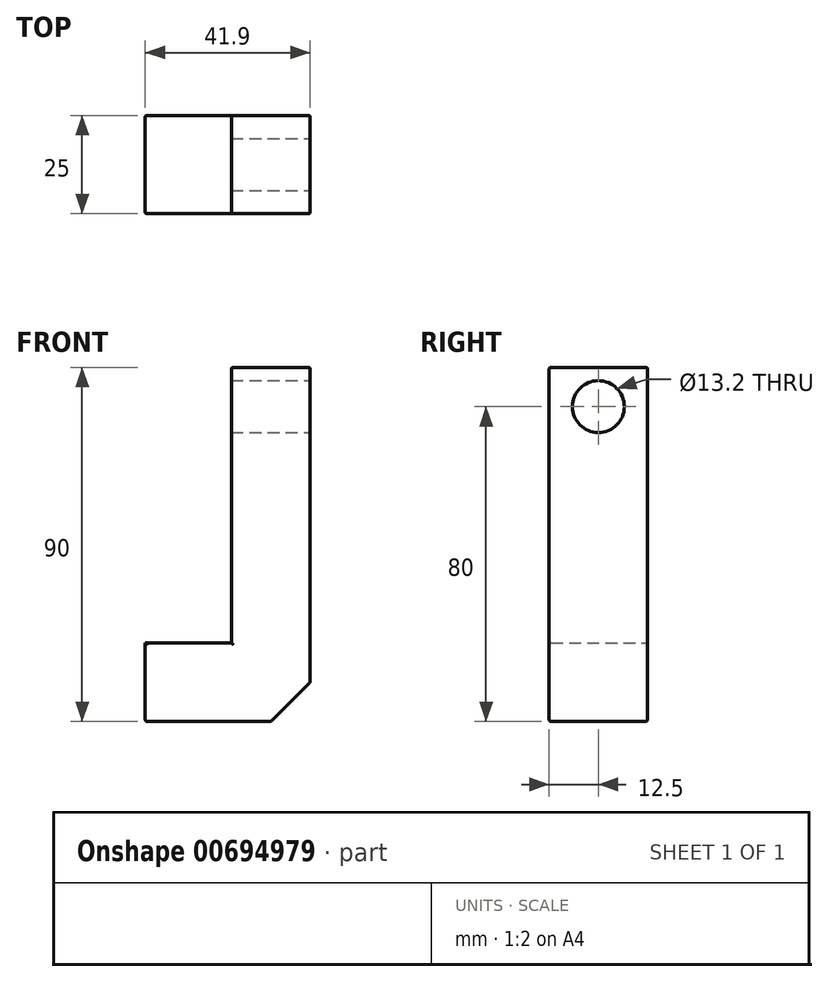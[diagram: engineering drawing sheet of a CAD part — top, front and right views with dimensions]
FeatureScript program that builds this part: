
annotation { "Feature Type Name" : "Feature", "Feature Type Description" : "" }
export const myFeature = defineFeature(function(context is Context, id is Id, definition is map)
    precondition{}
    {
        {
            var Q0;
            Q0=qCreatedBy(makeId("Front.planeOp"),FACE);
            var sketch = newSketch(context, id + "F0", { "sketchPlane" : qUnion([Q0])});
            skLineSegment(sketch, "E0", {"start": v(0, 0) * mm, "end": v(21.9, 0) * mm});
            skLineSegment(sketch, "E1", {"start": v(21.9, 0) * mm, "end": v(21.9, 70) * mm});
            skLineSegment(sketch, "E2", {"start": v(41.9, 70) * mm, "end": v(21.9, 70) * mm});
            skLineSegment(sketch, "E3", {"start": v(41.9, 70) * mm, "end": v(41.9, -20) * mm});
            skLineSegment(sketch, "E4", {"start": v(41.9, -20) * mm, "end": v(0, -20) * mm});
            skLineSegment(sketch, "E5", {"start": v(0, -20) * mm, "end": v(0, 0) * mm});
            skSolve(sketch);
        }
        {
            var Q0;
            Q0=makeQuery(id+"F0.imprint","IMPRINT",FACE,{"disambiguationData":[TD([[makeQuery(id+"F0.imprint","IMPRINT",EDGE,{"derivedFrom":sQuery(id+"F0.wireOp",EDGE,"E0")}),-1.0]])]});
            extrude(context, id + "F1", {"entities" : qUnion([Q0]), "depth" : 25 * mm, "offsetDistance" : 25 * mm});
        }
        {
            var Q0;
            Q0=makeQuery(id+"F1.opExtrude","SWEPT_EDGE",EDGE,{"disambiguationData":[OSD([sQuery(id+"F0.wireOp",EDGE,"E3"),sQuery(id+"F0.wireOp",EDGE,"E4")])]});
            chamfer(context, id + "F2", {"entities" : qUnion([Q0]), "width" : 10 * mm, "tangentPropagation" : true});
        }
        {
            var Q0;
            Q0=makeQuery(id+"F1.opExtrude","SWEPT_FACE",FACE,{"disambiguationData":[OSD([sQuery(id+"F0.wireOp",EDGE,"E3")])]});
            var sketch = newSketch(context, id + "F3", { "sketchPlane" : qUnion([Q0])});
            skPoint(sketch, "E6", {"position": v(-12.5, 60) * mm});
            skPoint(sketch, "E6.positionSnap0", {"position": v(-12.5, 70) * mm});
            skSolve(sketch);
        }
        {
            var Q0;
            Q0=sQuery(id+"F3.wireOp",VERTEX,"E6");
            var Q1;
            Q1=makeQuery(id+"F1.opExtrude","SWEPT_BODY",BODY,{"disambiguationData":[OSD([sQuery(id+"F0.wireOp",EDGE,"E0"),sQuery(id+"F0.wireOp",EDGE,"E1"),sQuery(id+"F0.wireOp",EDGE,"E2"),sQuery(id+"F0.wireOp",EDGE,"E3"),sQuery(id+"F0.wireOp",EDGE,"E4"),sQuery(id+"F0.wireOp",EDGE,"E5")])]});
            hole(context, id + "F4", {"style" : HoleStyle.SIMPLE, "endStyle" : HoleEndStyle.BLIND, "standardTappedOrClearance" : lookupTablePath({ "standard" : "ISO", "fit" : "Normal", "size" : "M12", "type" : "Clearance" }), "standardBlindInLast" : lookupTablePath({ "fit" : "Standard", "standard" : "ISO", "size" : "M12", "type" : "Clearance" }), "holeDiameter" : 13.2 * mm, "majorDiameter" : 10 * mm, "holeDepth" : 21 * mm, "isTappedThrough" : true, "tappedDepth" : 17.25 * mm, "tapClearance" : 3, "locations" : qUnion([Q0]), "scope" : qUnion([Q1])});
        }
        {
            var Q0;
            Q0=makeQuery(id+"F1.opExtrude","CAP_FACE",FACE,{"disambiguationData":[OSD([sQuery(id+"F0.wireOp",EDGE,"E0"),sQuery(id+"F0.wireOp",EDGE,"E1"),sQuery(id+"F0.wireOp",EDGE,"E2"),sQuery(id+"F0.wireOp",EDGE,"E3"),sQuery(id+"F0.wireOp",EDGE,"E4"),sQuery(id+"F0.wireOp",EDGE,"E5")])],"isStart":false});
            var Q1;
            Q1=makeQuery(id+"F1.opExtrude","CAP_FACE",FACE,{"disambiguationData":[OSD([sQuery(id+"F0.wireOp",EDGE,"E0"),sQuery(id+"F0.wireOp",EDGE,"E1"),sQuery(id+"F0.wireOp",EDGE,"E2"),sQuery(id+"F0.wireOp",EDGE,"E3"),sQuery(id+"F0.wireOp",EDGE,"E4"),sQuery(id+"F0.wireOp",EDGE,"E5")])],"isStart":true});
            var Q2;
            Q2=makeQuery(id+"F2.opChamfer","BLEND_FACE",FACE,{"disambiguationData":[OSD([sQuery(id+"F0.wireOp",EDGE,"E3"),sQuery(id+"F0.wireOp",EDGE,"E4")])]});
            var Q3;
            Q3=makeQuery(id+"F1.opExtrude","SWEPT_FACE",FACE,{"disambiguationData":[OSD([sQuery(id+"F0.wireOp",EDGE,"E4")])]});
            var Q4;
            Q4=makeQuery(id+"F1.opExtrude","SWEPT_FACE",FACE,{"disambiguationData":[OSD([sQuery(id+"F0.wireOp",EDGE,"E2")])]});
            var Q5;
            Q5=makeQuery(id+"F4.hole-0.boolean.opBoolean","INTERSECT",EDGE,{"derivedFrom":[makeQuery(id+"F1.opExtrude","SWEPT_FACE",FACE,{"disambiguationData":[OSD([sQuery(id+"F0.wireOp",EDGE,"E1")])]}),makeQuery(id+"F4.hole-0.opRevolve","SWEPT_FACE",FACE,{"disambiguationData":[OSD([sQuery(id+"F4.hole-0.sketch.wireOp",EDGE,"core_line_2")])]})]});
            var Q6;
            Q6=makeQuery(id+"F4.hole-0.boolean.opBoolean","COPY",FACE,{"derivedFrom":makeQuery(id+"F4.hole-0.opRevolve","SWEPT_FACE",FACE,{"disambiguationData":[OSD([sQuery(id+"F4.hole-0.sketch.wireOp",EDGE,"core_line_2")])]})});
            fillet(context, id + "F5", {"entities" : qUnion([Q0, Q1, Q2, Q3, Q4, Q5, Q6]), "radius" : .5 * mm, "tangentPropagation" : true, "allowEdgeOverflow" : false});
        }
    });
